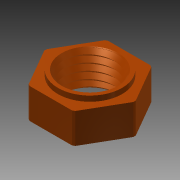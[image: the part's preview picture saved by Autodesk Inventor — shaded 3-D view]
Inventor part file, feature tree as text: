
AUTODESK INVENTOR PART (.ipt)
format: ipt  version: 2013 (Build 170138000, 138)  size: 231,424 bytes
history: native  units: mm
features: sketch x7, extrude x6, helix x1, projected_geometry x1
ambient origin geometry x8: Origin, YZ Plane, XZ Plane, XY Plane, X Axis, Y Axis, Z Axis, Center Point
bodies: Solid1 (feature_tree)
feature tree (15):
  extrude  "Extrusion1"  Depth=10.0mm TaperAngle=0.0deg
  extrude  "Extrusion2"  Depth=15.0mm TaperAngle=0.0deg
  helix  "Coil1"  [1 undecoded]
  extrude  "Extrusion8"  Depth=18.0mm
  extrude  "Extrusion9"  Depth=5.0mm
  extrude  "Extrusion10"  Depth=22.0mm
  extrude  "Extrusion11"  [1 undecoded]
  sketch  "Sketch1"  dims[d0=25.0mm d2=10.0mm d3=0.0mm]
  sketch  "Sketch2"  dims[d4=13.9mm d9=15.0mm d10=0.0mm d11=2.0mm]
  sketch  "Sketch3"  dims[d12=2.0001mm d13=10.0mm d14=100.0mm d15=0.0mm d16=90.0deg d17=90.0deg d18=0.0mm d19=0.0mm d47=18.0mm]
  sketch  "Sketch9"  dims[d49=1.5mm d50=0.0mm d51=5.0mm d52=-7.853982mm]
  sketch  "Sketch10"  dims[d53=5.0mm d54=-7.853982mm d55=22.0mm]
  sketch  "Sketch11"  dims[d56=0.0mm d57=0.0mm]
  sketch  "Sketch12"
  projected_geometry  "Project Cut Edges1"
note: 2 required parameter values undecoded (feature->parameter linkage not recoverable at this tier; creation-order binding heuristic only, values carry confidence <= 0.55)
